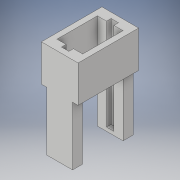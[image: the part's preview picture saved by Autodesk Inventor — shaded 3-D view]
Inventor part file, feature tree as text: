
AUTODESK INVENTOR PART (.ipt)
format: ipt  version: 2019 (Build 230136000, 136)  size: 154,112 bytes
history: native  units: mm
features: extrude x3, sketch x3
ambient origin geometry x8: Origin, YZ Plane, XZ Plane, XY Plane, X Axis, Y Axis, Z Axis, Center Point
bodies: Solid1 (feature_tree)
feature tree (6):
  extrude  "Extrusion1"  Depth=11.0mm
  extrude  "Extrusion2"  Depth=1.0mm
  extrude  "Extrusion3"  Depth=13.5mm
  sketch  "Sketch1"  dims[d0=2.0mm d1=11.0mm]
  sketch  "Sketch2"  dims[d2=5.5mm d3=1.0mm]
  sketch  "Sketch3"  dims[d5=2.5mm d6=13.5mm d7=1.5mm d8=25.0mm d9=0.0mm d10=1.5mm d11=10.0mm d12=0.0mm d13=1.0mm d14=0.0mm]
